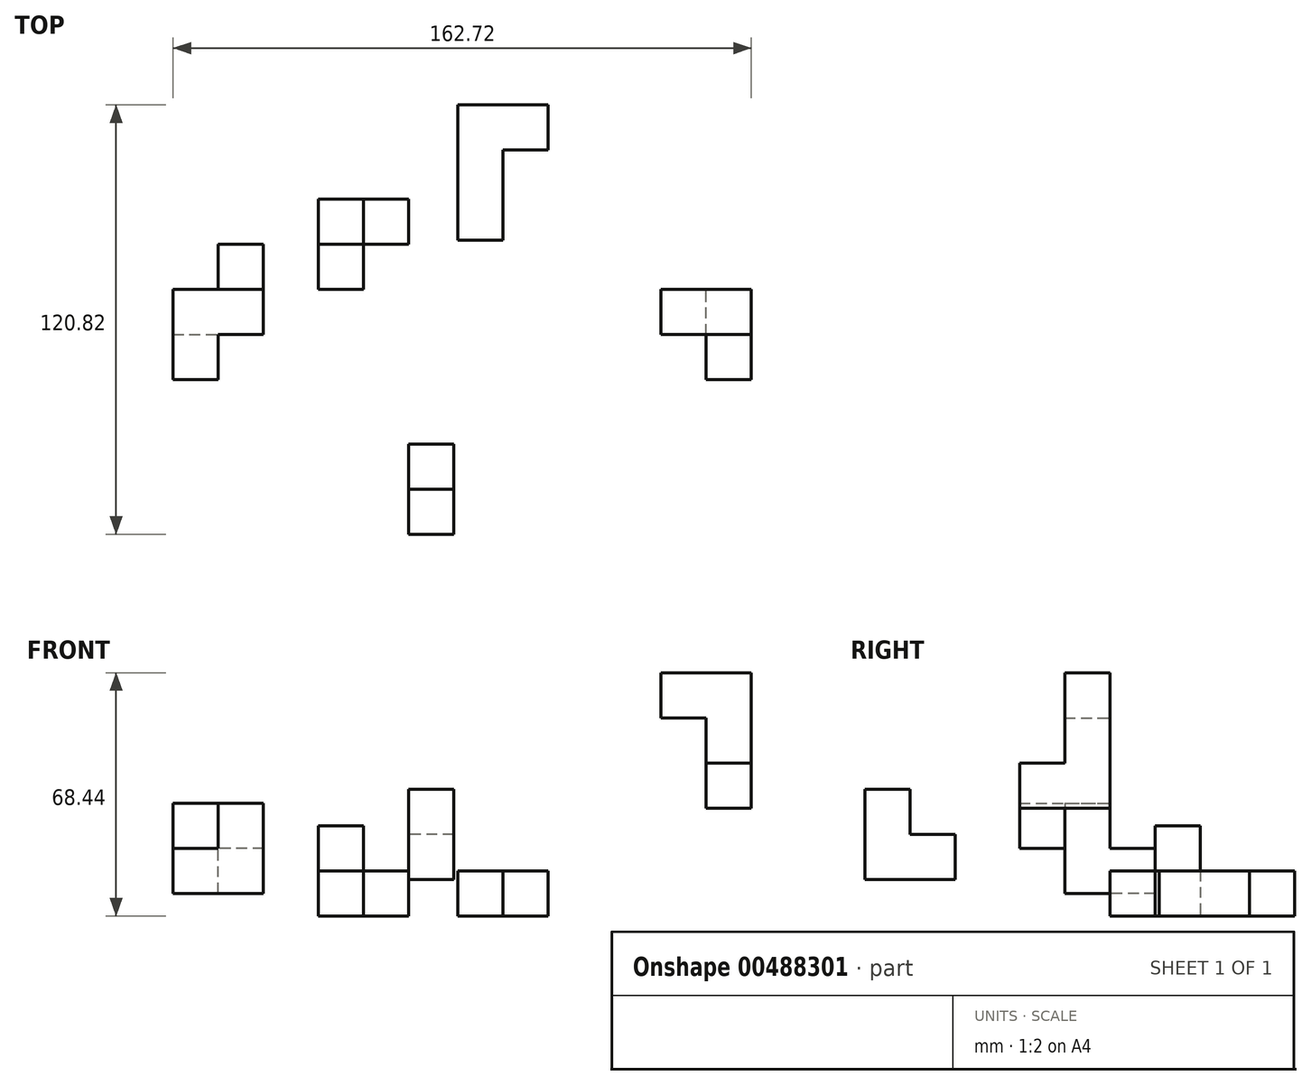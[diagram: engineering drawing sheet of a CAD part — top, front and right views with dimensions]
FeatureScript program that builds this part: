
annotation { "Feature Type Name" : "Feature", "Feature Type Description" : "" }
export const myFeature = defineFeature(function(context is Context, id is Id, definition is map)
    precondition{}
    {
        {
            var Q0;
            Q0=qCreatedBy(makeId("Top.planeOp"),FACE);
            var sketch = newSketch(context, id + "F0", { "sketchPlane" : qUnion([Q0])});
            skLineSegment(sketch, "E0", {"start": v(-25.4, 0) * mm, "end": v(-25.4, 25.4) * mm});
            skLineSegment(sketch, "E1", {"start": v(-25.4, 25.4) * mm, "end": v(0, 25.4) * mm});
            skLineSegment(sketch, "E2", {"start": v(0, 25.4) * mm, "end": v(0, 12.7) * mm});
            skLineSegment(sketch, "E3", {"start": v(0, 12.7) * mm, "end": v(-12.7, 12.7) * mm});
            skLineSegment(sketch, "E4", {"start": v(-12.7, 12.7) * mm, "end": v(-12.7, 0) * mm});
            skLineSegment(sketch, "E5", {"start": v(-12.7, 0) * mm, "end": v(-25.4, 0) * mm});
            skSolve(sketch);
        }
        {
            var Q0;
            Q0=makeQuery(id+"F0.imprint","IMPRINT",FACE,{"disambiguationData":[TD([[makeQuery(id+"F0.imprint","IMPRINT",EDGE,{"derivedFrom":sQuery(id+"F0.wireOp",EDGE,"E0")}),-1.0]])]});
            extrude(context, id + "F1", {"entities" : qUnion([Q0]), "depth" : 12.7 * mm});
        }
        {
            var Q0;
            Q0=makeQuery(id+"F1.opExtrude","CAP_FACE",FACE,{"disambiguationData":[OSD([sQuery(id+"F0.wireOp",EDGE,"E0"),sQuery(id+"F0.wireOp",EDGE,"E1"),sQuery(id+"F0.wireOp",EDGE,"E2"),sQuery(id+"F0.wireOp",EDGE,"E3"),sQuery(id+"F0.wireOp",EDGE,"E4"),sQuery(id+"F0.wireOp",EDGE,"E5")])],"isStart":false});
            var sketch = newSketch(context, id + "F2", { "sketchPlane" : qUnion([Q0])});
            skLineSegment(sketch, "E6.bottom", {"start": v(-25.4, 25.4) * mm, "end": v(-12.7, 25.4) * mm});
            skLineSegment(sketch, "E6.top", {"start": v(-25.4, 12.7) * mm, "end": v(-12.7, 12.7) * mm});
            skLineSegment(sketch, "E6.left", {"start": v(-25.4, 25.4) * mm, "end": v(-25.4, 12.7) * mm});
            skLineSegment(sketch, "E6.right", {"start": v(-12.7, 25.4) * mm, "end": v(-12.7, 12.7) * mm});
            skSolve(sketch);
        }
        {
            var Q0;
            Q0=makeQuery(id+"F2.imprint","IMPRINT",FACE,{"disambiguationData":[TD([[makeQuery(id+"F2.imprint","IMPRINT",EDGE,{"derivedFrom":sQuery(id+"F2.wireOp",EDGE,"E6.bottom")}),-1.0]])]});
            extrude(context, id + "F3", {"entities" : qUnion([Q0]), "operationType" : NewBodyOperationType.ADD, "depth" : 12.7 * mm});
        }
        {
            var Q0;
            Q0=qCreatedBy(makeId("Front.planeOp"),FACE);
            var sketch = newSketch(context, id + "F4", { "sketchPlane" : qUnion([Q0])});
            skLineSegment(sketch, "E7.bottom", {"start": v(83.79, 68.44) * mm, "end": v(96.49, 68.44) * mm});
            skLineSegment(sketch, "E7.top", {"start": v(83.79, 30.34) * mm, "end": v(96.49, 30.34) * mm});
            skLineSegment(sketch, "E7.left", {"start": v(83.79, 55.74) * mm, "end": v(83.79, 30.34) * mm});
            skLineSegment(sketch, "E7.right", {"start": v(96.49, 68.44) * mm, "end": v(96.49, 30.34) * mm});
            skLineSegment(sketch, "E8", {"start": v(83.79, 68.44) * mm, "end": v(71.09, 68.44) * mm});
            skLineSegment(sketch, "E9", {"start": v(71.09, 68.44) * mm, "end": v(71.09, 55.74) * mm});
            skLineSegment(sketch, "E10", {"start": v(71.09, 55.74) * mm, "end": v(83.79, 55.74) * mm});
            skSolve(sketch);
        }
        {
            var Q0;
            Q0=makeQuery(id+"F4.imprint","IMPRINT",FACE,{"disambiguationData":[TD([[makeQuery(id+"F4.imprint","IMPRINT",EDGE,{"derivedFrom":sQuery(id+"F4.wireOp",EDGE,"E7.bottom")}),-1.0]])]});
            extrude(context, id + "F5", {"entities" : qUnion([Q0]), "depth" : 12.7 * mm});
        }
        {
            var Q0;
            Q0=makeQuery(id+"F5.opExtrude","CAP_FACE",FACE,{"disambiguationData":[OSD([sQuery(id+"F4.wireOp",EDGE,"E7.bottom"),sQuery(id+"F4.wireOp",EDGE,"E7.top"),sQuery(id+"F4.wireOp",EDGE,"E7.left"),sQuery(id+"F4.wireOp",EDGE,"E7.right"),sQuery(id+"F4.wireOp",EDGE,"E8"),sQuery(id+"F4.wireOp",EDGE,"E9"),sQuery(id+"F4.wireOp",EDGE,"E10")])],"isStart":false});
            var sketch = newSketch(context, id + "F6", { "sketchPlane" : qUnion([Q0])});
            skLineSegment(sketch, "E11.bottom", {"start": v(83.79, 30.34) * mm, "end": v(96.49, 30.34) * mm});
            skLineSegment(sketch, "E11.top", {"start": v(83.79, 43.04) * mm, "end": v(96.49, 43.04) * mm});
            skLineSegment(sketch, "E11.left", {"start": v(83.79, 30.34) * mm, "end": v(83.79, 43.04) * mm});
            skLineSegment(sketch, "E11.right", {"start": v(96.49, 30.34) * mm, "end": v(96.49, 43.04) * mm});
            skSolve(sketch);
        }
        {
            var Q0;
            Q0=makeQuery(id+"F6.imprint","IMPRINT",FACE,{"disambiguationData":[TD([[makeQuery(id+"F6.imprint","IMPRINT",EDGE,{"derivedFrom":sQuery(id+"F6.wireOp",EDGE,"E11.bottom")}),1.0]])]});
            extrude(context, id + "F7", {"entities" : qUnion([Q0]), "operationType" : NewBodyOperationType.ADD, "depth" : 12.7 * mm});
        }
        {
            var Q0;
            Q0=qCreatedBy(makeId("Front.planeOp"),FACE);
            var sketch = newSketch(context, id + "F8", { "sketchPlane" : qUnion([Q0])});
            skLineSegment(sketch, "E12.bottom", {"start": v(-66.23, 31.76) * mm, "end": v(-40.83, 31.76) * mm});
            skLineSegment(sketch, "E12.top", {"start": v(-66.23, 6.36) * mm, "end": v(-40.83, 6.36) * mm});
            skLineSegment(sketch, "E12.left", {"start": v(-66.23, 31.76) * mm, "end": v(-66.23, 6.36) * mm});
            skLineSegment(sketch, "E12.right", {"start": v(-40.83, 31.76) * mm, "end": v(-40.83, 6.36) * mm});
            skSolve(sketch);
        }
        {
            var Q0;
            Q0=makeQuery(id+"F8.imprint","IMPRINT",FACE,{"disambiguationData":[TD([[makeQuery(id+"F8.imprint","IMPRINT",EDGE,{"derivedFrom":sQuery(id+"F8.wireOp",EDGE,"E12.bottom")}),-1.0]])]});
            extrude(context, id + "F9", {"entities" : qUnion([Q0]), "depth" : 12.7 * mm});
        }
        {
            var Q0;
            Q0=makeQuery(id+"F9.opExtrude","CAP_FACE",FACE,{"disambiguationData":[OSD([sQuery(id+"F8.wireOp",EDGE,"E12.bottom"),sQuery(id+"F8.wireOp",EDGE,"E12.top"),sQuery(id+"F8.wireOp",EDGE,"E12.left"),sQuery(id+"F8.wireOp",EDGE,"E12.right")])],"isStart":false});
            var sketch = newSketch(context, id + "F10", { "sketchPlane" : qUnion([Q0])});
            skLineSegment(sketch, "E13.bottom", {"start": v(-66.23, 31.76) * mm, "end": v(-53.53, 31.76) * mm});
            skLineSegment(sketch, "E13.top", {"start": v(-66.23, 19.06) * mm, "end": v(-53.53, 19.06) * mm});
            skLineSegment(sketch, "E13.left", {"start": v(-66.23, 31.76) * mm, "end": v(-66.23, 19.06) * mm});
            skLineSegment(sketch, "E13.right", {"start": v(-53.53, 31.76) * mm, "end": v(-53.53, 19.06) * mm});
            skSolve(sketch);
        }
        {
            var Q0;
            Q0=makeQuery(id+"F10.imprint","IMPRINT",FACE,{"disambiguationData":[TD([[makeQuery(id+"F10.imprint","IMPRINT",EDGE,{"derivedFrom":sQuery(id+"F10.wireOp",EDGE,"E13.bottom")}),-1.0]])]});
            extrude(context, id + "F11", {"entities" : qUnion([Q0]), "operationType" : NewBodyOperationType.ADD, "depth" : 12.7 * mm});
        }
        {
            var Q0;
            Q0=makeQuery(id+"F9.opExtrude","CAP_FACE",FACE,{"disambiguationData":[OSD([sQuery(id+"F8.wireOp",EDGE,"E12.bottom"),sQuery(id+"F8.wireOp",EDGE,"E12.top"),sQuery(id+"F8.wireOp",EDGE,"E12.left"),sQuery(id+"F8.wireOp",EDGE,"E12.right")])],"isStart":true});
            var sketch = newSketch(context, id + "F12", { "sketchPlane" : qUnion([Q0])});
            skLineSegment(sketch, "E14.bottom", {"start": v(40.83, 6.36) * mm, "end": v(53.53, 6.36) * mm});
            skLineSegment(sketch, "E14.top", {"start": v(40.83, 19.06) * mm, "end": v(53.53, 19.06) * mm});
            skLineSegment(sketch, "E14.left", {"start": v(40.83, 6.36) * mm, "end": v(40.83, 19.06) * mm});
            skLineSegment(sketch, "E14.right", {"start": v(53.53, 6.36) * mm, "end": v(53.53, 19.06) * mm});
            skSolve(sketch);
        }
        {
            var Q0;
            Q0=makeQuery(id+"F12.imprint","IMPRINT",FACE,{"disambiguationData":[TD([[makeQuery(id+"F12.imprint","IMPRINT",EDGE,{"derivedFrom":sQuery(id+"F12.wireOp",EDGE,"E14.bottom")}),-1.0]])]});
            extrude(context, id + "F13", {"entities" : qUnion([Q0]), "operationType" : NewBodyOperationType.ADD, "depth" : 12.7 * mm});
        }
        {
            var Q0;
            Q0=qCreatedBy(makeId("Top.planeOp"),FACE);
            var sketch = newSketch(context, id + "F14", { "sketchPlane" : qUnion([Q0])});
            skLineSegment(sketch, "E15", {"start": v(13.85, 13.84) * mm, "end": v(13.85, 51.94) * mm});
            skLineSegment(sketch, "E16", {"start": v(13.85, 51.94) * mm, "end": v(39.25, 51.94) * mm});
            skLineSegment(sketch, "E17", {"start": v(39.25, 51.94) * mm, "end": v(39.25, 39.24) * mm});
            skLineSegment(sketch, "E18", {"start": v(39.25, 39.24) * mm, "end": v(26.55, 39.24) * mm});
            skLineSegment(sketch, "E19", {"start": v(26.55, 39.24) * mm, "end": v(26.55, 13.84) * mm});
            skLineSegment(sketch, "E20", {"start": v(26.55, 13.84) * mm, "end": v(13.85, 13.84) * mm});
            skSolve(sketch);
        }
        {
            var Q0;
            Q0=makeQuery(id+"F14.imprint","IMPRINT",FACE,{"disambiguationData":[TD([[makeQuery(id+"F14.imprint","IMPRINT",EDGE,{"derivedFrom":sQuery(id+"F14.wireOp",EDGE,"E15")}),-1.0]])]});
            extrude(context, id + "F15", {"entities" : qUnion([Q0]), "depth" : 12.7 * mm});
        }
        {
            var Q0;
            Q0=qCreatedBy(makeId("Right.planeOp"),FACE);
            var sketch = newSketch(context, id + "F16", { "sketchPlane" : qUnion([Q0])});
            skLineSegment(sketch, "E21", {"start": v(-68.88, 35.66) * mm, "end": v(-56.18, 35.66) * mm});
            skLineSegment(sketch, "E22", {"start": v(-56.18, 35.66) * mm, "end": v(-56.18, 22.96) * mm});
            skLineSegment(sketch, "E23", {"start": v(-56.18, 22.96) * mm, "end": v(-43.48, 22.96) * mm});
            skLineSegment(sketch, "E24", {"start": v(-43.48, 22.96) * mm, "end": v(-43.48, 10.26) * mm});
            skLineSegment(sketch, "E25", {"start": v(-43.48, 10.26) * mm, "end": v(-68.88, 10.26) * mm});
            skLineSegment(sketch, "E26", {"start": v(-68.88, 10.26) * mm, "end": v(-68.88, 35.66) * mm});
            skSolve(sketch);
        }
        {
            var Q0;
            Q0=makeQuery(id+"F16.imprint","IMPRINT",FACE,{"disambiguationData":[TD([[makeQuery(id+"F16.imprint","IMPRINT",EDGE,{"derivedFrom":sQuery(id+"F16.wireOp",EDGE,"E21")}),-1.0]])]});
            extrude(context, id + "F17", {"entities" : qUnion([Q0]), "depth" : 12.7 * mm});
        }
    });
